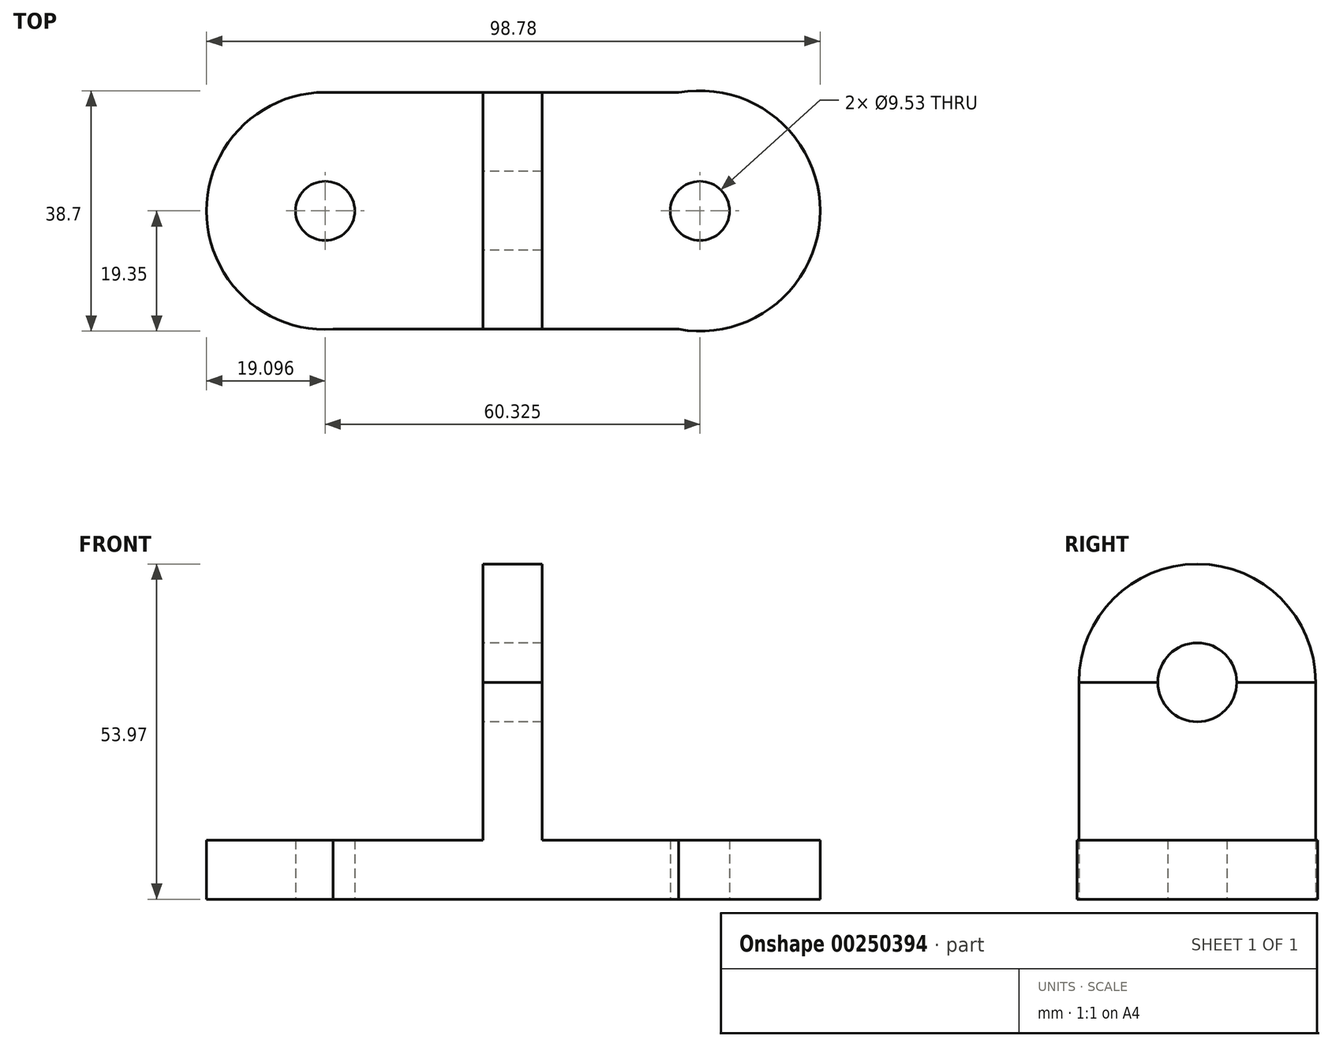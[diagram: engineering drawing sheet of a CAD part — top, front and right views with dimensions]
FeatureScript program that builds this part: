
annotation { "Feature Type Name" : "Feature", "Feature Type Description" : "" }
export const myFeature = defineFeature(function(context is Context, id is Id, definition is map)
    precondition{}
    {
        {
            var Q0;
            Q0=qCreatedBy(makeId("Top.planeOp"),FACE);
            var sketch = newSketch(context, id + "F0", { "sketchPlane" : qUnion([Q0])});
            skLineSegment(sketch, "E0", {"start": v(-51.91, 19.05) * mm, "end": v(8.41, 19.05) * mm});
            skLineSegment(sketch, "E1", {"start": v(8.41, -19.05) * mm, "end": v(-51.91, -19.05) * mm});
            skPoint(sketch, "E2.end.orphan", {"position": v(8.41, 0) * mm});
            skPoint(sketch, "E2.start.orphan", {"position": v(-51.91, 0) * mm});
            skArc(sketch, "E3", {"start": v(-50.64, 19.05) * mm, "mid": v(-71, 0) * mm, "end": v(-50.64, -19.05) * mm});
            skArc(sketch, "E4", {"start": v(5, -19.05) * mm, "mid": v(27.77, 0) * mm, "end": v(5, 19.05) * mm});
            skCircle(sketch, "E5", {"center": v(-51.91, 0) * mm, "radius": 4.76 * mm});
            skCircle(sketch, "E6", {"center": v(8.41, 0) * mm, "radius": 4.76 * mm});
            skSolve(sketch);
        }
        {
            var Q0;
            Q0 = qSketchRegion(id + "F0", true);
            extrude(context, id + "F1", {"entities" : qUnion([Q0]), "depth" : 9.52 * mm});
        }
        {
            var Q0;
            Q0=makeQuery(id+"F1.opExtrude","CAP_FACE",FACE,{"disambiguationData":[OSD([sQuery(id+"F0.wireOp",EDGE,"E0"),sQuery(id+"F0.wireOp",EDGE,"E1"),sQuery(id+"F0.wireOp",EDGE,"E3"),sQuery(id+"F0.wireOp",EDGE,"E4"),sQuery(id+"F0.wireOp",EDGE,"E5"),sQuery(id+"F0.wireOp",EDGE,"E6")])],"isStart":false});
            var sketch = newSketch(context, id + "F2", { "sketchPlane" : qUnion([Q0])});
            skLineSegment(sketch, "E7", {"start": v(-26.51, 0) * mm, "end": v(-26.51, -19.05) * mm});
            skLineSegment(sketch, "E8", {"start": v(-26.51, 0) * mm, "end": v(-26.51, 19.05) * mm});
            skLineSegment(sketch, "E9", {"start": v(-16.99, 0) * mm, "end": v(-16.99, -19.05) * mm});
            skLineSegment(sketch, "E10", {"start": v(-16.99, -19.05) * mm, "end": v(-16.99, 19.05) * mm});
            skPoint(sketch, "E11.start.orphan", {"position": v(-51.91, 0) * mm});
            skLineSegment(sketch, "E12", {"start": v(-16.99, 19.05) * mm, "end": v(-26.51, 19.05) * mm});
            skLineSegment(sketch, "E13", {"start": v(-26.51, 19.05) * mm, "end": v(-16.99, 19.05) * mm});
            skLineSegment(sketch, "E14", {"start": v(-16.99, -19.05) * mm, "end": v(-26.51, -19.05) * mm});
            skSolve(sketch);
        }
        {
            var Q0;
            Q0=makeQuery(id+"F2.imprint","IMPRINT",FACE,{"disambiguationData":[TD([[makeQuery(id+"F2.imprint","IMPRINT",EDGE,{"derivedFrom":sQuery(id+"F2.wireOp",EDGE,"E7")}),1.0]])]});
            extrude(context, id + "F3", {"entities" : qUnion([Q0]), "operationType" : NewBodyOperationType.ADD, "depth" : 25.4 * mm});
        }
        {
            var Q0;
            Q0=makeQuery(id+"F3.opExtrude","SWEPT_FACE",FACE,{"disambiguationData":[OSD([sQuery(id+"F2.wireOp",EDGE,"E10")])]});
            var sketch = newSketch(context, id + "F4", { "sketchPlane" : qUnion([Q0])});
            skPoint(sketch, "E15.center.orphan", {"position": v(0, 34.93) * mm});
            skArc(sketch, "E16", {"start": v(19.05, 34.93) * mm, "mid": v(0, 53.98) * mm, "end": v(-19.05, 34.93) * mm});
            skSolve(sketch);
        }
        {
            var Q0;
            Q0 = qSketchRegion(id + "F4", true);
            var Q1;
            Q1=makeQuery(id+"F4.imprint","IMPRINT",FACE,{"disambiguationData":[TD([[makeQuery(id+"F4.imprint","IMPRINT",EDGE,{"derivedFrom":sQuery(id+"F4.wireOp",EDGE,"E16")}),1.0]])]});
            extrude(context, id + "F5", {"entities" : qUnion([Q0, Q1]), "oppositeDirection" : true, "depth" : 9.52 * mm});
        }
        {
            var Q0;
            Q0=makeQuery(id+"F5.opExtrude","CAP_FACE",FACE,{"disambiguationData":[OSD([sQuery(id+"F2.wireOp",EDGE,"E10"),sQuery(id+"F4.wireOp",EDGE,"E16")])],"isStart":false});
            var sketch = newSketch(context, id + "F6", { "sketchPlane" : qUnion([Q0])});
            skPoint(sketch, "E17.center.orphan", {"position": v(0, 34.93) * mm});
            skLineSegment(sketch, "E18", {"start": v(-19.05, 34.93) * mm, "end": v(0, 34.93) * mm});
            skSolve(sketch);
        }
        {
            var Q0;
            Q0=sQuery(id+"F6.wireOp",VERTEX,"E17.center.orphan");
            var Q1;
            Q1=makeQuery(id+"F1.opExtrude","SWEPT_BODY",BODY,{"disambiguationData":[OSD([sQuery(id+"F0.wireOp",EDGE,"E0"),sQuery(id+"F0.wireOp",EDGE,"E1"),sQuery(id+"F0.wireOp",EDGE,"E3"),sQuery(id+"F0.wireOp",EDGE,"E4"),sQuery(id+"F0.wireOp",EDGE,"E5"),sQuery(id+"F0.wireOp",EDGE,"E6")])]});
            var Q2;
            Q2=makeQuery(id+"F5.opExtrude","SWEPT_BODY",BODY,{"disambiguationData":[OSD([sQuery(id+"F2.wireOp",EDGE,"E10"),sQuery(id+"F4.wireOp",EDGE,"E16")])]});
            hole(context, id + "F7", {"style" : HoleStyle.SIMPLE, "endStyle" : HoleEndStyle.THROUGH, "holeDiameter" : 12.7 * mm, "tappedDepth" : 12.7 * mm, "tapClearance" : 3, "locations" : qUnion([Q0]), "scope" : qUnion([Q1, Q2])});
        }
    });
